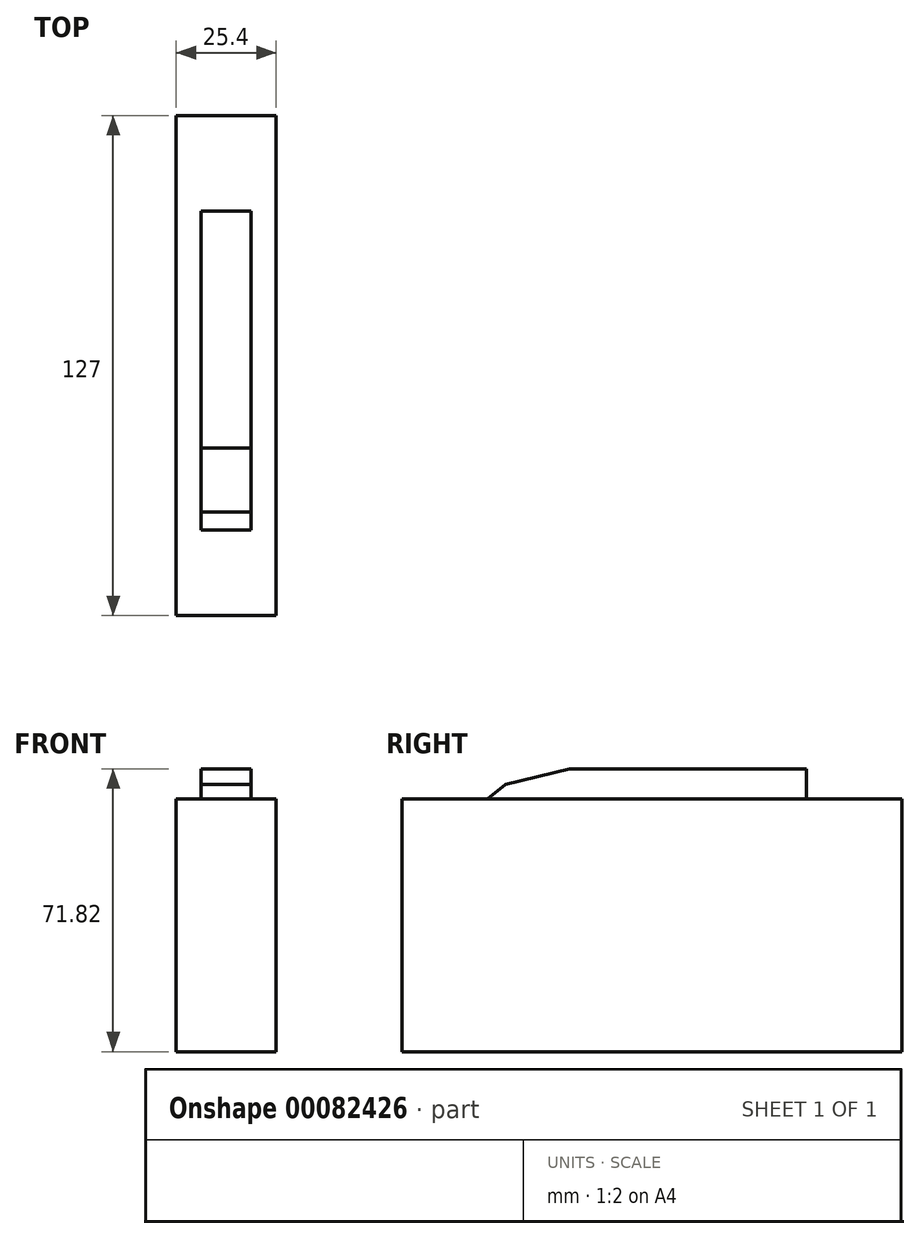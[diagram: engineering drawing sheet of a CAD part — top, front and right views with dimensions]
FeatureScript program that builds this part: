
annotation { "Feature Type Name" : "Feature", "Feature Type Description" : "" }
export const myFeature = defineFeature(function(context is Context, id is Id, definition is map)
    precondition{}
    {
        {
            var Q0;
            Q0=qCreatedBy(makeId("Front.planeOp"),FACE);
            var sketch = newSketch(context, id + "F0", { "sketchPlane" : qUnion([Q0])});
            skLineSegment(sketch, "E0.bottom", {"start": v(12.7, 38.1) * mm, "end": v(-12.7, 38.1) * mm});
            skLineSegment(sketch, "E0.top", {"start": v(12.7, -38.1) * mm, "end": v(-12.7, -38.1) * mm});
            skLineSegment(sketch, "E0.left", {"start": v(12.7, 38.1) * mm, "end": v(12.7, -38.1) * mm});
            skLineSegment(sketch, "E0.right", {"start": v(-12.7, 38.1) * mm, "end": v(-12.7, -38.1) * mm});
            skPoint(sketch, "E0.middle", {"position": v(0, 0) * mm});
            skSolve(sketch);
        }
        {
            var Q0;
            Q0 = qSketchRegion(id + "F0", true);
            extrude(context, id + "F1", {"entities" : qUnion([Q0]), "depth" : 127 * mm});
        }
        {
            var Q0;
            Q0=makeQuery(id+"F1.opExtrude","CAP_FACE",FACE,{"disambiguationData":[OSD([sQuery(id+"F0.wireOp",EDGE,"E0.bottom"),sQuery(id+"F0.wireOp",EDGE,"E0.top"),sQuery(id+"F0.wireOp",EDGE,"E0.left"),sQuery(id+"F0.wireOp",EDGE,"E0.right")])],"isStart":false});
            var sketch = newSketch(context, id + "F2", { "sketchPlane" : qUnion([Q0])});
            skLineSegment(sketch, "E1", {"start": v(12.7, 26.1) * mm, "end": v(6.35, 26.1) * mm});
            skLineSegment(sketch, "E2.top", {"start": v(-6.35, 33.72) * mm, "end": v(6.35, 33.72) * mm});
            skLineSegment(sketch, "E2.left", {"start": v(-6.35, 26.1) * mm, "end": v(-6.35, 33.72) * mm});
            skLineSegment(sketch, "E2.right", {"start": v(6.35, 26.1) * mm, "end": v(6.35, 33.72) * mm});
            skLineSegment(sketch, "E3.trimOffspring", {"start": v(-6.35, 26.1) * mm, "end": v(-12.7, 26.1) * mm});
            skSolve(sketch);
        }
        {
            var Q0;
            {var subQ0=sQuery(id+"F2.wireOp",EDGE,"E1");Q0=makeQuery(id+"F2.imprint","IMPRINT",FACE,{"disambiguationData":[TD([[makeQuery(id+"F2.imprint","IMPRINT",EDGE,{"derivedFrom":subQ0}),-1.0]])]});}
            extrude(context, id + "F3", {"entities" : qUnion([Q0]), "operationType" : NewBodyOperationType.REMOVE, "oppositeDirection" : true, "depth" : 177.8 * mm});
        }
        {
            var Q0;
            Q0=makeQuery(id+"F3.boolean.opBoolean","COPY",FACE,{"derivedFrom":makeQuery(id+"F3.opExtrude","SWEPT_FACE",FACE,{"disambiguationData":[OSD([sQuery(id+"F2.wireOp",EDGE,"E2.right")])]})});
            var sketch = newSketch(context, id + "F4", { "sketchPlane" : qUnion([Q0])});
            skLineSegment(sketch, "E4", {"start": v(-84.44, 33.72) * mm, "end": v(-100.7, 29.8) * mm});
            skLineSegment(sketch, "E5", {"start": v(-100.7, 29.8) * mm, "end": v(-105.27, 26.1) * mm});
            skLineSegment(sketch, "E6", {"start": v(-105.27, 26.1) * mm, "end": v(-24.26, 26.1) * mm});
            skLineSegment(sketch, "E7", {"start": v(-24.26, 26.1) * mm, "end": v(-24.26, 33.72) * mm});
            skLineSegment(sketch, "E8", {"start": v(-24.26, 33.72) * mm, "end": v(-84.44, 33.72) * mm});
            skSolve(sketch);
        }
        {
            var Q0;
            {var subQ4=sQuery(id+"F4.wireOp",EDGE,"E4");Q0=makeQuery(id+"F4.imprint","IMPRINT",FACE,{"disambiguationData":[TD([[makeQuery(id+"F4.imprint","IMPRINT",EDGE,{"derivedFrom":subQ4}),-1.0]])]});}
            var Q1;
            {var subQ0=sQuery(id+"F4.wireOp",EDGE,"E7");Q1=makeQuery(id+"F4.imprint","IMPRINT",FACE,{"disambiguationData":[TD([[makeQuery(id+"F4.imprint","IMPRINT",EDGE,{"derivedFrom":subQ0}),-1.0]])]});}
            extrude(context, id + "F5", {"entities" : qUnion([Q0, Q1]), "operationType" : NewBodyOperationType.REMOVE, "oppositeDirection" : true, "depth" : 25.4 * mm});
        }
    });
